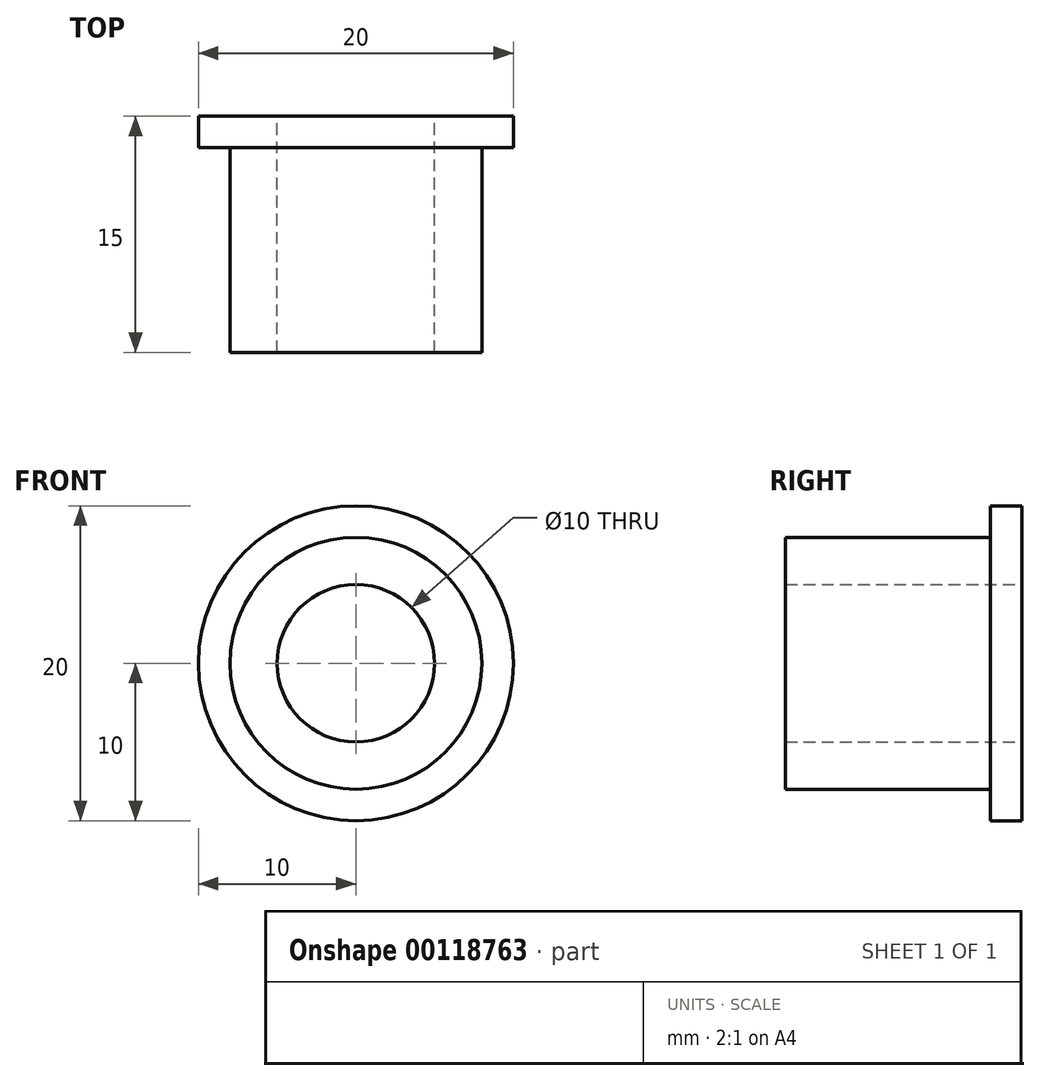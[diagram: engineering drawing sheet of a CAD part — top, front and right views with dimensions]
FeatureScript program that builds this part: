
annotation { "Feature Type Name" : "Feature", "Feature Type Description" : "" }
export const myFeature = defineFeature(function(context is Context, id is Id, definition is map)
    precondition{}
    {
        {
            var Q0;
            Q0=qCreatedBy(makeId("Front.planeOp"),FACE);
            var sketch = newSketch(context, id + "F0", { "sketchPlane" : qUnion([Q0])});
            skCircle(sketch, "E0", {"center": v(0, 0) * mm, "radius": 8 * mm});
            skCircle(sketch, "E1", {"center": v(0, 0) * mm, "radius": 5 * mm});
            skSolve(sketch);
        }
        {
            var Q0;
            Q0 = qSketchRegion(id + "F0", true);
            extrude(context, id + "F1", {"entities" : qUnion([Q0]), "depth" : 13 * mm});
        }
        {
            var Q0;
            Q0=makeQuery(id+"F1.opExtrude","CAP_FACE",FACE,{"disambiguationData":[OSD([sQuery(id+"F0.wireOp",EDGE,"E0"),sQuery(id+"F0.wireOp",EDGE,"E1")])],"isStart":true});
            var sketch = newSketch(context, id + "F2", { "sketchPlane" : qUnion([Q0])});
            skCircle(sketch, "E2", {"center": v(0, 0) * mm, "radius": 10 * mm});
            skCircle(sketch, "E3", {"center": v(0, 0) * mm, "radius": 5 * mm});
            skSolve(sketch);
        }
        {
            var Q0;
            Q0 = qSketchRegion(id + "F2", true);
            extrude(context, id + "F3", {"entities" : qUnion([Q0]), "operationType" : NewBodyOperationType.ADD, "depth" : 2 * mm});
        }
    });
